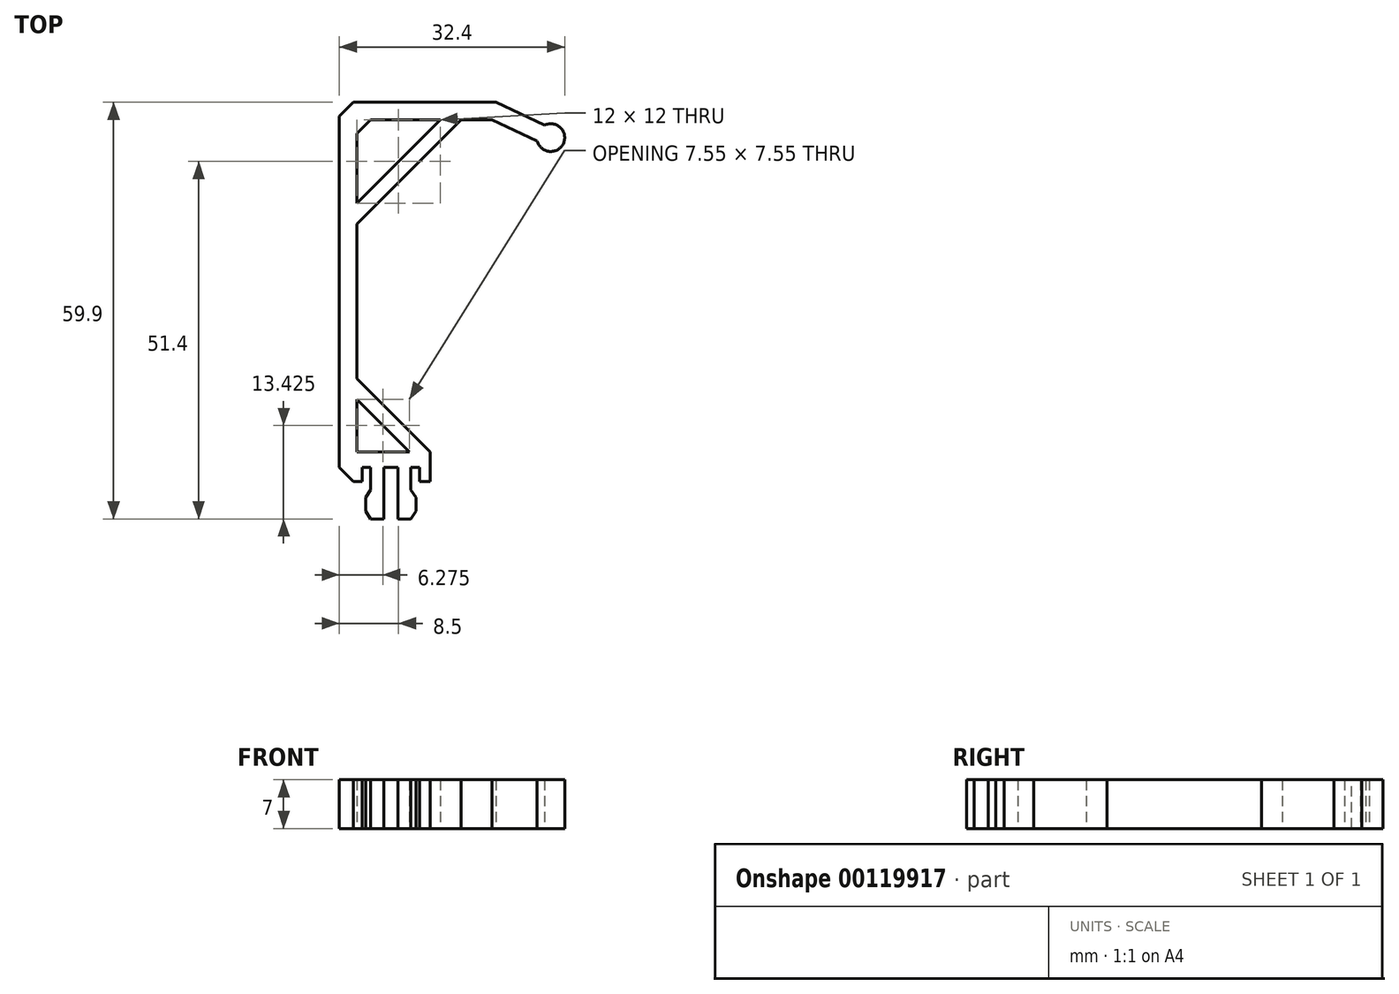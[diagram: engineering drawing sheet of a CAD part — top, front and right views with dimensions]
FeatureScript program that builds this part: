
annotation { "Feature Type Name" : "Feature", "Feature Type Description" : "" }
export const myFeature = defineFeature(function(context is Context, id is Id, definition is map)
    precondition{}
    {
        {
            var Q0;
            Q0=qCreatedBy(makeId("Top.planeOp"),FACE);
            var sketch = newSketch(context, id + "F0", { "sketchPlane" : qUnion([Q0])});
            skLineSegment(sketch, "E0.bottom", {"start": v(-1, 0) * mm, "end": v(-2.9, 0) * mm});
            skLineSegment(sketch, "E0.top", {"start": v(-1, -7.4) * mm, "end": v(-2.9, -7.4) * mm});
            skLineSegment(sketch, "E0.left", {"start": v(-1, 0) * mm, "end": v(-1, -7.4) * mm});
            skLineSegment(sketch, "E0.right", {"start": v(-2.9, 0) * mm, "end": v(-2.9, -7.4) * mm});
            skLineSegment(sketch, "E1", {"start": v(-2.9, -7.4) * mm, "end": v(-3.6, -6.3) * mm});
            skLineSegment(sketch, "E2", {"start": v(-3.6, -6.3) * mm, "end": v(-3.6, -4.3) * mm});
            skLineSegment(sketch, "E3", {"start": v(-3.6, -4.3) * mm, "end": v(-2.9, -3.2) * mm});
            skLineSegment(sketch, "E4.MirrorCS", {"start": v(1, 0) * mm, "end": v(2.9, 0) * mm});
            skLineSegment(sketch, "E5.MirrorCS", {"start": v(3.6, -4.3) * mm, "end": v(2.9, -3.2) * mm});
            skLineSegment(sketch, "E6.MirrorCS", {"start": v(1, -7.4) * mm, "end": v(2.9, -7.4) * mm});
            skLineSegment(sketch, "E7.MirrorCS", {"start": v(1, 0) * mm, "end": v(1, -7.4) * mm});
            skLineSegment(sketch, "E8.MirrorCS", {"start": v(2.9, 0) * mm, "end": v(2.9, -7.4) * mm});
            skLineSegment(sketch, "E9.MirrorCS", {"start": v(2.9, -7.4) * mm, "end": v(3.6, -6.3) * mm});
            skLineSegment(sketch, "E10.MirrorCS", {"start": v(3.6, -6.3) * mm, "end": v(3.6, -4.3) * mm});
            skLineSegment(sketch, "E11", {"start": v(1, 0) * mm, "end": v(-1, 0) * mm});
            skLineSegment(sketch, "E12", {"start": v(2.9, 0) * mm, "end": v(4.15, 0) * mm});
            skLineSegment(sketch, "E13", {"start": v(4.15, 0) * mm, "end": v(4.15, -2) * mm});
            skLineSegment(sketch, "E14", {"start": v(4.15, -2) * mm, "end": v(5.65, -2) * mm});
            skLineSegment(sketch, "E15", {"start": v(5.65, -2) * mm, "end": v(5.65, 2.25) * mm});
            skLineSegment(sketch, "E16", {"start": v(2.65, 2.25) * mm, "end": v(-4.9, 2.25) * mm});
            skLineSegment(sketch, "E17", {"start": v(-2.9, 0) * mm, "end": v(-4.15, 0) * mm});
            skLineSegment(sketch, "E18", {"start": v(-4.15, 0) * mm, "end": v(-4.15, -2) * mm});
            skLineSegment(sketch, "E19", {"start": v(-4.15, -2) * mm, "end": v(-7.4, -2) * mm});
            skLineSegment(sketch, "E20", {"start": v(-7.4, -2) * mm, "end": v(-7.4, 52.5) * mm});
            skLineSegment(sketch, "E21", {"start": v(-4.9, 2.25) * mm, "end": v(-4.9, 9.8) * mm});
            skLineSegment(sketch, "E22", {"start": v(-4.9, 50) * mm, "end": v(14.55, 50) * mm});
            skLineSegment(sketch, "E23", {"start": v(5.65, 2.25) * mm, "end": v(-4.9, 12.8) * mm});
            skLineSegment(sketch, "E24", {"start": v(2.65, 2.25) * mm, "end": v(-4.9, 9.8) * mm});
            skLineSegment(sketch, "E25.trimOffspring", {"start": v(-4.9, 12.8) * mm, "end": v(-4.9, 50) * mm});
            skLineSegment(sketch, "E26", {"start": v(-4.9, 38) * mm, "end": v(7.1, 50) * mm});
            skLineSegment(sketch, "E27", {"start": v(10.1, 50) * mm, "end": v(-4.9, 35) * mm});
            skLineSegment(sketch, "E28", {"start": v(14.55, 50) * mm, "end": v(22.48, 46.3) * mm});
            skLineSegment(sketch, "E29", {"start": v(22.48, 46.3) * mm, "end": v(23.53, 48.57) * mm});
            skLineSegment(sketch, "E30", {"start": v(23.53, 48.57) * mm, "end": v(15.1, 52.5) * mm});
            skLineSegment(sketch, "E31", {"start": v(15.1, 52.5) * mm, "end": v(-7.4, 52.5) * mm});
            skCircle(sketch, "E32", {"center": v(23, 47.43) * mm, "radius": 2 * mm});
            skSolve(sketch);
        }
        {
            var Q0;
            Q0 = qSketchRegion(id + "F0", true);
            extrude(context, id + "F1", {"entities" : qUnion([Q0]), "depth" : 7 * mm});
        }
        {
            var Q0;
            Q0=makeQuery(id+"F1.opExtrude","SWEPT_EDGE",EDGE,{"disambiguationData":[OSD([sQuery(id+"F0.wireOp",EDGE,"E20"),sQuery(id+"F0.wireOp",EDGE,"0dllHYmb-7COt-ttak-97sy-ixv086gSsBnm")])]});
            var Q1;
            Q1=makeQuery(id+"F1.opExtrude","SWEPT_EDGE",EDGE,{"disambiguationData":[OSD([sQuery(id+"F0.wireOp",EDGE,"E22"),sQuery(id+"F0.wireOp",EDGE,"E25.trimOffspring")])]});
            chamfer(context, id + "F2", {"entities" : qUnion([Q0, Q1]), "width" : 2 * mm, "tangentPropagation" : true});
        }
    });
